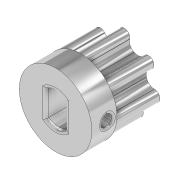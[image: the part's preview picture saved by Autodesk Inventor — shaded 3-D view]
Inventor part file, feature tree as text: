
AUTODESK INVENTOR PART (.ipt)
format: ipt  version: 2020 (Build 240168000, 168)  size: 401,920 bytes
history: native  units: in
note: dims shown in document units (in); Inventor stores cm internally (conversion verified against a paired STEP export)
features: chamfer x7, extrude x4, sketch x4, fillet x3, projected_geometry x1
ambient origin geometry x8: Origin, YZ Plane, XZ Plane, XY Plane, X Axis, Y Axis, Z Axis, Center Point
bodies: Solid1 (feature_tree)
feature tree (19):
  extrude  "Extrusion1"  Depth=0.4724in
  extrude  "Extrusion2"  Depth=0.084in
  extrude  "Extrusion3"  Depth=0.084in
  fillet  "Fillet1"  Radius=2.7559in
  chamfer  "Chamfer3"  Distance=0.2362in
  chamfer  "Chamfer4"  Distance=0.1969in
  chamfer  "Chamfer5"  Distance=0.1575in
  chamfer  "Chamfer6"  Distance=0.0118in
  chamfer  "Chamfer7"  Distance=0.0079in
  chamfer  "Chamfer8"  Distance=0.0394in Angle=45.0deg
  chamfer  "Chamfer9"  Distance=0.0394in Angle=45.0deg
  extrude  "Extrusion4"  Depth=0.0118in TaperAngle=45.0deg
  fillet  "Fillet2"  Radius=0.0394in
  fillet  "Fillet3"  Radius=0.0394in
  sketch  "Sketch1"  dims[d0=0.2047in d1=0.4724in]
  sketch  "Sketch2"  dims[d2=0.0866in d5=0.084in]
  sketch  "Sketch3"  dims[d6=0.084in d7=0.084in d8=2.7559in d10=360.0deg d12=0.2362in d13=0.0in d14=0.1969in d15=0.0in]
  sketch  "Sketch4"  dims[d16=0.0748in d17=0.1575in d18=0.0in d22=0.0118in d23=0.0079in d28=0.0394in d29=0.0866in d30=45.0deg d31=0.0394in d32=0.0866in d33=45.0deg d34=0.0394in d35=0.0866in d36=45.0deg d37=0.0394in d38=0.0866in d39=45.0deg d40=0.0394in d41=0.0866in d42=45.0deg d43=0.0394in d44=0.0866in d45=45.0deg d46=0.0394in d47=0.0866in d48=45.0deg d49=0.122in d50=0.061in d51=1.0in d52=0.0in d53=0.0197in d54=0.0118in d24=0.5in d25=0.0344in d26=0.5in d27=0.0344in]
  projected_geometry  "Projected Loop1"
